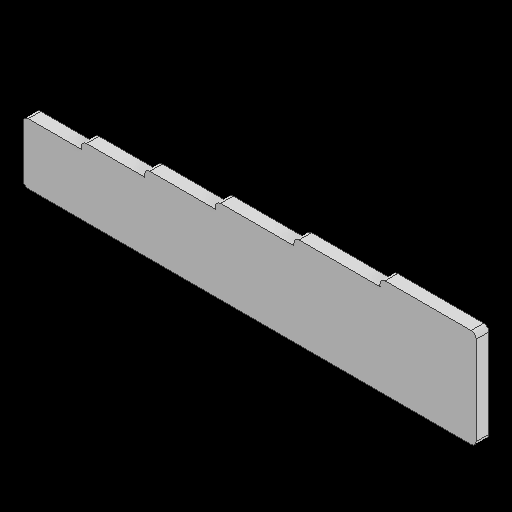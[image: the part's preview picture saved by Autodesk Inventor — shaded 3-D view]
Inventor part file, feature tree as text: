
AUTODESK INVENTOR PART (.ipt)
format: ipt  version: 2025.1 (Build 291241000, 241)  size: 210,432 bytes
history: native  units: in
note: dims shown in document units (in); Inventor stores cm internally (conversion verified against a paired STEP export)
features: extrude x2, sketch x2, other x1, fillet x1, projected_geometry x1
ambient origin geometry x8: Origin, YZ Plane, XZ Plane, XY Plane, X Axis, Y Axis, Z Axis, Center Point
bodies: Body1 (feature_tree)
feature tree (7):
  other  "솔리드1"
  extrude  "돌출1"  Depth=0.7874in
  extrude  "돌출2"  Depth=0.7874in
  fillet  "모깎기1"  Radius=0.0787in
  sketch  "스케치1"
  sketch  "스케치2"
  projected_geometry  "투영된 루프1"
